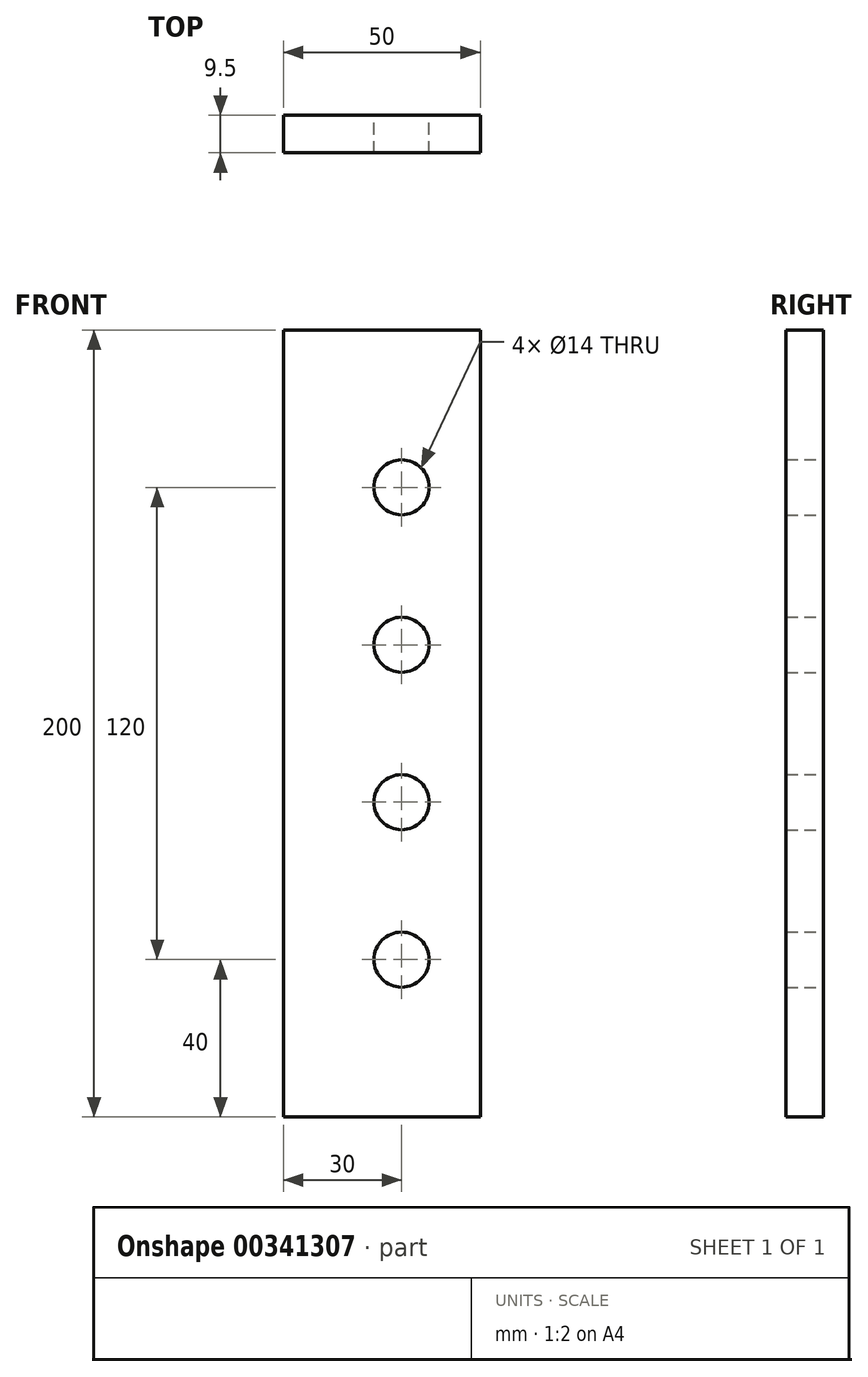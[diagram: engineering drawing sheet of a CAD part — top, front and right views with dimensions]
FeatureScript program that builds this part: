
annotation { "Feature Type Name" : "Feature", "Feature Type Description" : "" }
export const myFeature = defineFeature(function(context is Context, id is Id, definition is map)
    precondition{}
    {
        {
            var Q0;
            Q0=qCreatedBy(makeId("Front.planeOp"),FACE);
            var sketch = newSketch(context, id + "F0", { "sketchPlane" : qUnion([Q0])});
            skLineSegment(sketch, "E0.bottom", {"start": v(0, 0) * mm, "end": v(50, 0) * mm});
            skLineSegment(sketch, "E0.top", {"start": v(0, 200) * mm, "end": v(50, 200) * mm});
            skLineSegment(sketch, "E0.left", {"start": v(0, 0) * mm, "end": v(0, 200) * mm});
            skLineSegment(sketch, "E0.right", {"start": v(50, 0) * mm, "end": v(50, 200) * mm});
            skSolve(sketch);
        }
        {
            var Q0;
            Q0=makeQuery(id+"F0.imprint","IMPRINT",FACE,{"disambiguationData":[TD([[makeQuery(id+"F0.imprint","IMPRINT",EDGE,{"derivedFrom":sQuery(id+"F0.wireOp",EDGE,"E0.bottom")}),1.0]])]});
            extrude(context, id + "F1", {"entities" : qUnion([Q0]), "depth" : 9.5 * mm});
        }
        {
            var Q0;
            Q0=makeQuery(id+"F1.opExtrude","CAP_FACE",FACE,{"disambiguationData":[OSD([sQuery(id+"F0.wireOp",EDGE,"E0.bottom"),sQuery(id+"F0.wireOp",EDGE,"E0.top"),sQuery(id+"F0.wireOp",EDGE,"E0.left"),sQuery(id+"F0.wireOp",EDGE,"E0.right")])],"isStart":false});
            var sketch = newSketch(context, id + "F2", { "sketchPlane" : qUnion([Q0])});
            skLineSegment(sketch, "E1", {"start": v(30, 200) * mm, "end": v(30, 0) * mm});
            skPoint(sketch, "E2", {"position": v(30, 160) * mm});
            skPoint(sketch, "E3", {"position": v(30, 120) * mm});
            skPoint(sketch, "E4", {"position": v(30, 80) * mm});
            skPoint(sketch, "E5", {"position": v(30, 40) * mm});
            skSolve(sketch);
        }
        {
            var Q0;
            Q0=sQuery(id+"F2.wireOp",VERTEX,"E2");
            var Q1;
            Q1=sQuery(id+"F2.wireOp",VERTEX,"E3");
            var Q2;
            Q2=sQuery(id+"F2.wireOp",VERTEX,"E4");
            var Q3;
            Q3=sQuery(id+"F2.wireOp",VERTEX,"E5");
            var Q4;
            Q4=makeQuery(id+"F1.opExtrude","SWEPT_BODY",BODY,{"disambiguationData":[OSD([sQuery(id+"F0.wireOp",EDGE,"E0.bottom"),sQuery(id+"F0.wireOp",EDGE,"E0.top"),sQuery(id+"F0.wireOp",EDGE,"E0.left"),sQuery(id+"F0.wireOp",EDGE,"E0.right")])]});
            hole(context, id + "F3", {"style" : HoleStyle.SIMPLE, "endStyle" : HoleEndStyle.THROUGH, "holeDiameter" : 14 * mm, "tappedDepth" : 12 * mm, "tapClearance" : 3, "locations" : qUnion([Q0, Q1, Q2, Q3]), "scope" : qUnion([Q4]), "startStyle" : HoleStartStyle.PART});
        }
    });
